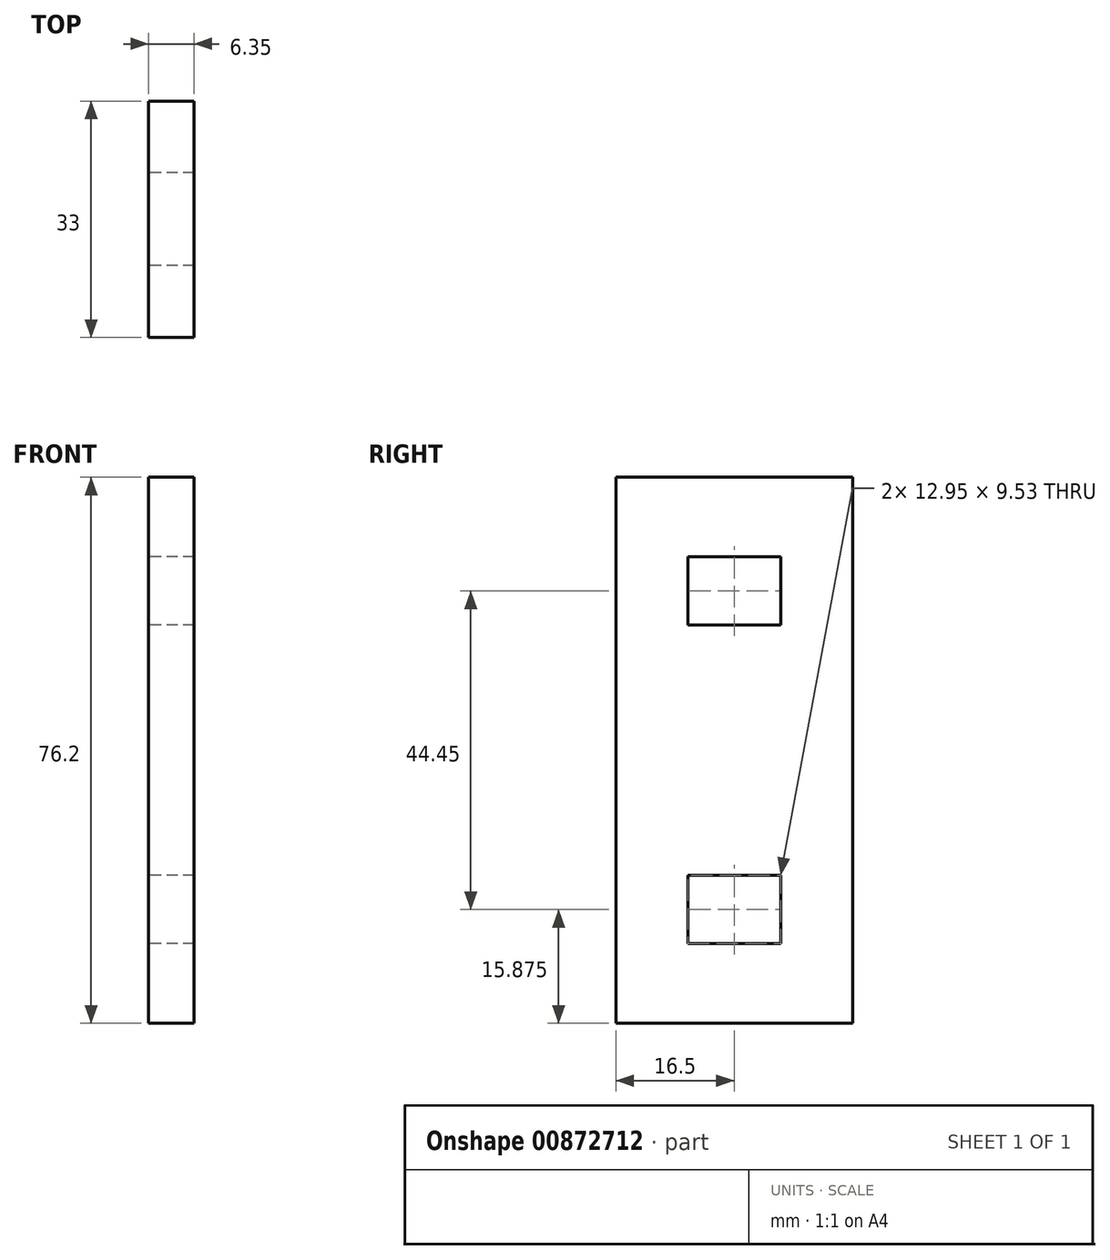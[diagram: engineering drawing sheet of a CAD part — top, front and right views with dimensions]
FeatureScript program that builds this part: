
annotation { "Feature Type Name" : "Feature", "Feature Type Description" : "" }
export const myFeature = defineFeature(function(context is Context, id is Id, definition is map)
    precondition{}
    {
        {
            var Q0;
            Q0=qCreatedBy(makeId("Right.planeOp"),FACE);
            var sketch = newSketch(context, id + "F0", { "sketchPlane" : qUnion([Q0])});
            skLineSegment(sketch, "E0.bottom", {"start": v(-16.5, 3.17) * mm, "end": v(16.5, 3.17) * mm});
            skLineSegment(sketch, "E0.top", {"start": v(-16.5, -3.18) * mm, "end": v(16.5, -3.18) * mm});
            skLineSegment(sketch, "E0.left", {"start": v(-16.5, 3.18) * mm, "end": v(-16.5, -3.18) * mm});
            skLineSegment(sketch, "E0.right", {"start": v(16.5, 3.17) * mm, "end": v(16.5, -3.18) * mm});
            skPoint(sketch, "E0.middle", {"position": v(0, 0) * mm});
            skLineSegment(sketch, "E1.0", {"start": v(-34.3, 22.23) * mm, "end": v(34.3, 22.23) * mm, "construction": true});
            skLineSegment(sketch, "E2.MirrorCS", {"start": v(-34.3, -22.23) * mm, "end": v(34.3, -22.23) * mm, "construction": true});
            skLineSegment(sketch, "E3.bottom", {"start": v(-6.48, 17.46) * mm, "end": v(6.48, 17.46) * mm});
            skLineSegment(sketch, "E3.top", {"start": v(-6.48, 26.99) * mm, "end": v(6.48, 26.99) * mm});
            skLineSegment(sketch, "E3.left", {"start": v(-6.48, 17.46) * mm, "end": v(-6.48, 26.99) * mm});
            skLineSegment(sketch, "E3.right", {"start": v(6.48, 17.46) * mm, "end": v(6.48, 26.99) * mm});
            skPoint(sketch, "E3.middle", {"position": v(0, 22.23) * mm});
            skLineSegment(sketch, "E4.MirrorCS", {"start": v(-6.48, -17.46) * mm, "end": v(-6.48, -26.99) * mm});
            skLineSegment(sketch, "E5.MirrorCS", {"start": v(-6.48, -26.99) * mm, "end": v(6.48, -26.99) * mm});
            skLineSegment(sketch, "E6.MirrorCS", {"start": v(-6.48, -17.46) * mm, "end": v(6.48, -17.46) * mm});
            skPoint(sketch, "E7.MirrorP", {"position": v(0, -22.23) * mm});
            skLineSegment(sketch, "E8.MirrorCS", {"start": v(6.48, -17.46) * mm, "end": v(6.48, -26.99) * mm});
            skLineSegment(sketch, "E9.bottom", {"start": v(-16.5, 38.1) * mm, "end": v(16.5, 38.1) * mm});
            skLineSegment(sketch, "E9.top", {"start": v(-16.5, -38.1) * mm, "end": v(16.5, -38.1) * mm});
            skLineSegment(sketch, "E9.left", {"start": v(-16.5, 38.1) * mm, "end": v(-16.5, -38.1) * mm});
            skLineSegment(sketch, "E9.right", {"start": v(16.5, 38.1) * mm, "end": v(16.5, -38.1) * mm});
            skLineSegment(sketch, "E10", {"start": v(0, 38.1) * mm, "end": v(0, -38.1) * mm, "construction": true});
            skSolve(sketch);
        }
        {
            var Q0;
            Q0=makeQuery(id+"F0.imprint","IMPRINT",FACE,{"disambiguationData":[TD([[makeQuery(id+"F0.imprint","IMPRINT",EDGE,{"derivedFrom":sQuery(id+"F0.wireOp",EDGE,"E0.bottom")}),-1.0]])]});
            var Q1;
            {var subQ1=sQuery(id+"F0.wireOp",EDGE,"E0.bottom");Q1=makeQuery(id+"F0.imprint","IMPRINT",FACE,{"disambiguationData":[TD([[makeQuery(id+"F0.imprint","IMPRINT",EDGE,{"derivedFrom":subQ1}),1.0]])]});}
            var Q2;
            {var subQ0=sQuery(id+"F0.wireOp",EDGE,"E0.top");Q2=makeQuery(id+"F0.imprint","IMPRINT",FACE,{"disambiguationData":[TD([[makeQuery(id+"F0.imprint","IMPRINT",EDGE,{"derivedFrom":subQ0}),-1.0]])]});}
            extrude(context, id + "F1", {"entities" : qUnion([Q0, Q1, Q2]), "depth" : 6.35 * mm, "offsetDistance" : 25.4 * mm});
        }
    });
